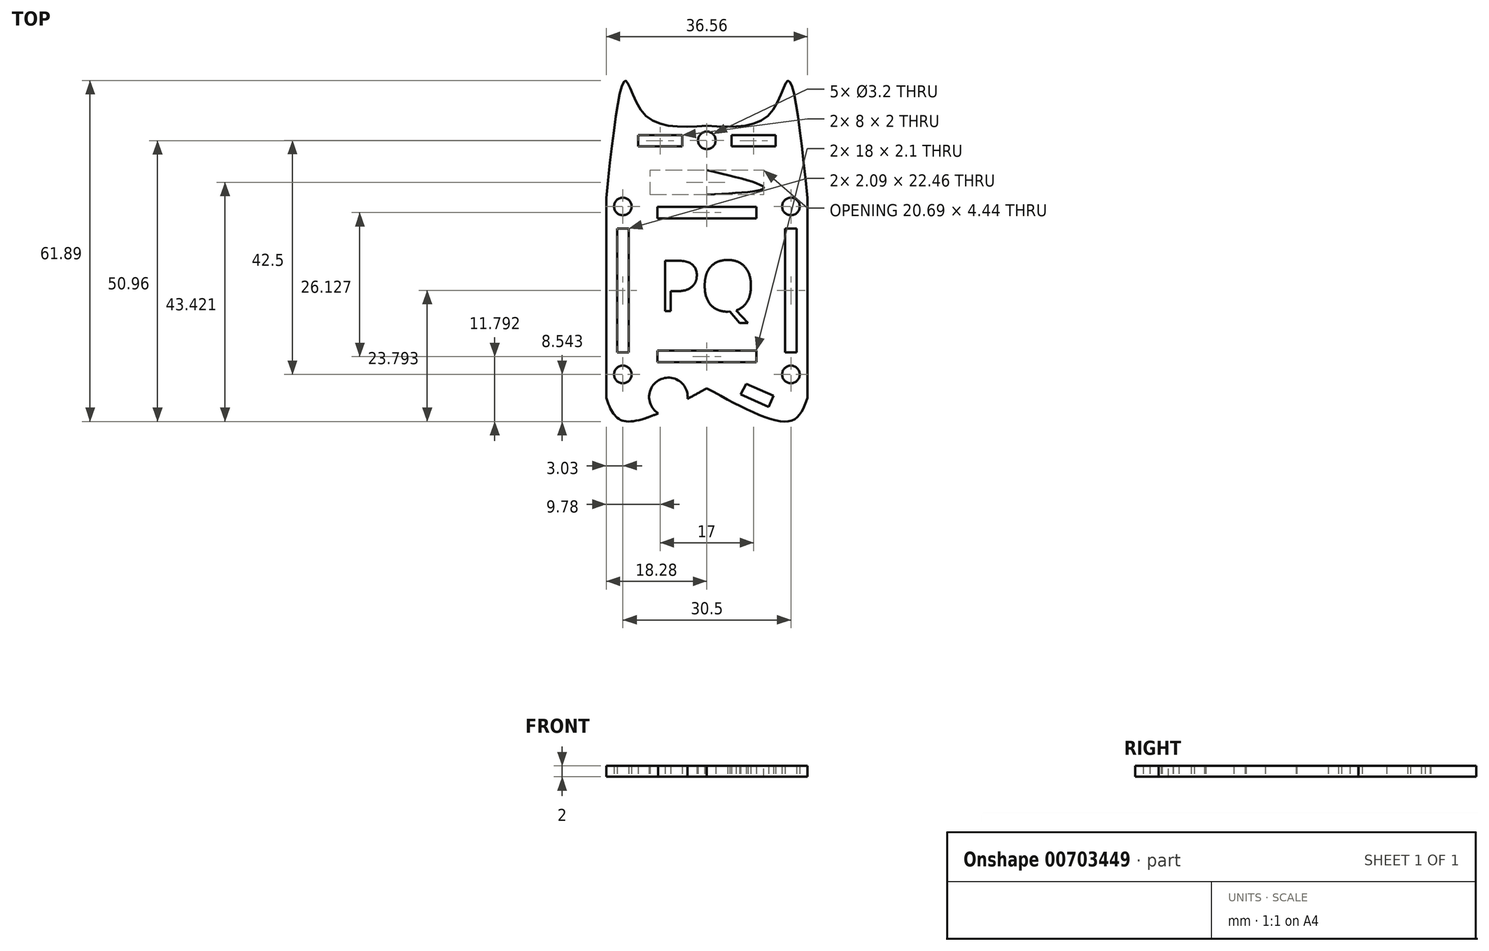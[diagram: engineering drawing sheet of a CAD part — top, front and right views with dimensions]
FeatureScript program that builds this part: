
annotation { "Feature Type Name" : "Feature", "Feature Type Description" : "" }
export const myFeature = defineFeature(function(context is Context, id is Id, definition is map)
    precondition{}
    {
        {
            var Q0;
            Q0=qCreatedBy(makeId("Top.planeOp"),FACE);
            var sketch = newSketch(context, id + "F0", { "sketchPlane" : qUnion([Q0])});
            skCircle(sketch, "E0.MirrorC", {"center": v(13.1, 8.4) * mm, "radius": 1.6 * mm});
            skCircle(sketch, "E1.MirrorC", {"center": v(43.6, 8.4) * mm, "radius": 1.6 * mm});
            skCircle(sketch, "E2.MirrorC", {"center": v(43.6, 38.9) * mm, "radius": 1.6 * mm});
            skCircle(sketch, "E3.MirrorC", {"center": v(13.1, 38.9) * mm, "radius": 1.6 * mm});
            skPoint(sketch, "E4", {"position": v(28.35, 38.9) * mm});
            skPoint(sketch, "E5.orphan", {"position": v(15.2, 38.07) * mm});
            skPoint(sketch, "E6.orphan", {"position": v(14.92, 50.26) * mm});
            skPoint(sketch, "E7.MirrorP", {"position": v(39.77, 55.59) * mm});
            skPoint(sketch, "E8.MirrorP", {"position": v(40.3, 38.07) * mm});
            skPoint(sketch, "E9", {"position": v(28.35, 50.9) * mm});
            skCircle(sketch, "E10", {"center": v(28.35, 50.9) * mm, "radius": 1.6 * mm});
            skPoint(sketch, "E11", {"position": v(32.85, 51.82) * mm});
            skLineSegment(sketch, "E12", {"start": v(32.85, 51.82) * mm, "end": v(32.85, 49.82) * mm});
            skLineSegment(sketch, "E13.MirrorCS", {"start": v(23.85, 51.82) * mm, "end": v(23.85, 49.82) * mm});
            skPoint(sketch, "E14", {"position": v(40.85, 51.82) * mm});
            skLineSegment(sketch, "E15", {"start": v(40.85, 51.82) * mm, "end": v(40.85, 49.82) * mm});
            skLineSegment(sketch, "E16.MirrorCS", {"start": v(15.85, 51.82) * mm, "end": v(15.85, 49.82) * mm});
            skLineSegment(sketch, "E17.trimOffspring", {"start": v(15.85, 51.82) * mm, "end": v(23.85, 51.82) * mm});
            skLineSegment(sketch, "E18", {"start": v(15.85, 49.82) * mm, "end": v(23.85, 49.82) * mm});
            skLineSegment(sketch, "E19", {"start": v(32.85, 51.82) * mm, "end": v(40.85, 51.82) * mm});
            skLineSegment(sketch, "E20", {"start": v(32.85, 49.82) * mm, "end": v(40.85, 49.82) * mm});
            skLineSegment(sketch, "E21", {"start": v(23.85, 49.82) * mm, "end": v(35.95, 49.82) * mm});
            skPoint(sketch, "E22", {"position": v(43.6, 23.65) * mm});
            skLineSegment(sketch, "E23.left", {"start": v(10.07, 40.38) * mm, "end": v(10.07, 4.12) * mm});
            skLineSegment(sketch, "E23.right", {"start": v(46.63, 40.38) * mm, "end": v(46.63, 4.12) * mm});
            skFitSpline(sketch, "E24", {"points": [v(10.07, 4.12) * mm, v(13.1, 0) * mm, v(28.35, 5.89) * mm], "startDerivative": vector(5.7, -15.2) * mm, "endDerivative": vector(28.7, 15.81) * mm});
            skFitSpline(sketch, "E25.MirrorCS", {"points": [v(46.63, 4.12) * mm, v(43.6, 0) * mm, v(28.35, 5.89) * mm], "startDerivative": vector(-5.7, -15.2) * mm, "endDerivative": vector(-28.7, 15.81) * mm});
            skPoint(sketch, "E26.orphan", {"position": v(46.63, 65.65) * mm});
            skPoint(sketch, "E27.orphan", {"position": v(10.07, 65.65) * mm});
            skPoint(sketch, "E28.orphan", {"position": v(10.07, -18.35) * mm});
            skPoint(sketch, "E29.orphan", {"position": v(46.63, -18.35) * mm});
            skCircle(sketch, "E30", {"center": v(21.36, 4.31) * mm, "radius": 3.5 * mm});
            skLineSegment(sketch, "E31", {"start": v(28.35, 23.65) * mm, "end": v(28.35, 32.54) * mm});
            skLineSegment(sketch, "E32.bottom", {"start": v(28.35, 38.83) * mm, "end": v(37.35, 38.83) * mm});
            skLineSegment(sketch, "E32.top", {"start": v(28.35, 36.73) * mm, "end": v(37.35, 36.73) * mm});
            skLineSegment(sketch, "E32.left", {"start": v(28.35, 38.83) * mm, "end": v(28.35, 36.73) * mm});
            skLineSegment(sketch, "E32.right", {"start": v(37.35, 38.83) * mm, "end": v(37.35, 36.73) * mm});
            skLineSegment(sketch, "E33.bottom", {"start": v(28.35, 12.7) * mm, "end": v(37.35, 12.7) * mm});
            skLineSegment(sketch, "E33.top", {"start": v(28.35, 10.6) * mm, "end": v(37.35, 10.6) * mm});
            skLineSegment(sketch, "E33.left", {"start": v(28.35, 12.7) * mm, "end": v(28.35, 10.6) * mm});
            skLineSegment(sketch, "E33.right", {"start": v(37.35, 12.7) * mm, "end": v(37.35, 10.6) * mm});
            skLineSegment(sketch, "E34.bottom", {"start": v(44.64, 34.88) * mm, "end": v(42.56, 34.88) * mm});
            skLineSegment(sketch, "E34.top", {"start": v(44.64, 12.42) * mm, "end": v(42.56, 12.42) * mm});
            skLineSegment(sketch, "E34.left", {"start": v(44.64, 34.88) * mm, "end": v(44.64, 12.42) * mm});
            skLineSegment(sketch, "E34.right", {"start": v(42.56, 34.88) * mm, "end": v(42.56, 12.42) * mm});
            skLineSegment(sketch, "E35.MirrorCS", {"start": v(19.35, 38.83) * mm, "end": v(19.35, 36.73) * mm});
            skPoint(sketch, "E36.MirrorP", {"position": v(13.1, 23.65) * mm});
            skLineSegment(sketch, "E37.MirrorCS", {"start": v(14.14, 34.88) * mm, "end": v(14.14, 12.42) * mm});
            skPoint(sketch, "E38.MirrorP", {"position": v(16.4, 38.07) * mm});
            skLineSegment(sketch, "E39.MirrorCS", {"start": v(12.06, 34.88) * mm, "end": v(14.14, 34.88) * mm});
            skLineSegment(sketch, "E40.MirrorCS", {"start": v(28.35, 12.7) * mm, "end": v(19.35, 12.7) * mm});
            skLineSegment(sketch, "E41.MirrorCS", {"start": v(28.35, 38.83) * mm, "end": v(19.35, 38.83) * mm});
            skLineSegment(sketch, "E42.MirrorCS", {"start": v(19.35, 12.7) * mm, "end": v(19.35, 10.6) * mm});
            skLineSegment(sketch, "E43.MirrorCS", {"start": v(28.35, 10.6) * mm, "end": v(19.35, 10.6) * mm});
            skLineSegment(sketch, "E44.MirrorCS", {"start": v(12.06, 12.42) * mm, "end": v(14.14, 12.42) * mm});
            skLineSegment(sketch, "E45.MirrorCS", {"start": v(28.35, 36.73) * mm, "end": v(19.35, 36.73) * mm});
            skLineSegment(sketch, "E46.MirrorCS", {"start": v(12.06, 34.88) * mm, "end": v(12.06, 12.42) * mm});
            skLineSegment(sketch, "E47", {"start": v(34.48, 4.76) * mm, "end": v(39.57, 2.5) * mm});
            skLineSegment(sketch, "E48", {"start": v(39.57, 2.5) * mm, "end": v(40.46, 4.53) * mm});
            skLineSegment(sketch, "E49", {"start": v(40.46, 4.53) * mm, "end": v(35.52, 6.72) * mm});
            skLineSegment(sketch, "E50", {"start": v(35.52, 6.72) * mm, "end": v(34.48, 4.76) * mm});
            skArc(sketch, "E51", {"start": v(17.07, 0.4) * mm, "mid": v(23.87, -0.92) * mm, "end": v(27.1, 5.2) * mm});
            skText(sketch, "E52", { "text": "PQ ", "fontName": "OpenSans-Regular.ttf"});
            skFitSpline(sketch, "E53", {"points": [v(10.07, 40.38) * mm, v(13.62, 61.74) * mm, v(16.95, 55.68) * mm, v(28.35, 53.53) * mm], "startDerivative": vector(8, 74.86) * mm, "endDerivative": vector(42.02, 2.44) * mm});
            skFitSpline(sketch, "E54", {"points": [v(28.35, 41.06) * mm, v(18, 42.28) * mm, v(28.35, 45.5) * mm], "startDerivative": vector(-31.13, 1.49) * mm, "endDerivative": vector(30.93, 7.38) * mm});
            skFitSpline(sketch, "E55.MirrorCS", {"points": [v(28.35, 41.06) * mm, v(38.7, 42.28) * mm, v(28.35, 45.5) * mm], "startDerivative": vector(31.13, 1.49) * mm, "endDerivative": vector(-30.93, 7.38) * mm});
            skFitSpline(sketch, "E56.MirrorCS", {"points": [v(46.63, 40.38) * mm, v(43.08, 61.74) * mm, v(39.75, 55.68) * mm, v(28.35, 53.53) * mm], "startDerivative": vector(-8, 74.86) * mm, "endDerivative": vector(-42.02, 2.44) * mm});
            const initialGuessF0  = {"E52": [0.01948, 0.01992, 1, 0, 0.0092]};
            skSetInitialGuess(sketch, initialGuessF0);
            skSolve(sketch);
        }
        {
            var Q0;
            Q0=makeQuery(id+"F0.imprint","IMPRINT",FACE,{"disambiguationData":[TD([[makeQuery(id+"F0.imprint","IMPRINT",EDGE,{"derivedFrom":sQuery(id+"F0.wireOp",EDGE,"E0.MirrorC")}),-1.0]])]});
            extrude(context, id + "F1", {"entities" : qUnion([Q0]), "depth" : 2 * mm, "offsetDistance" : 25 * mm});
        }
    });
